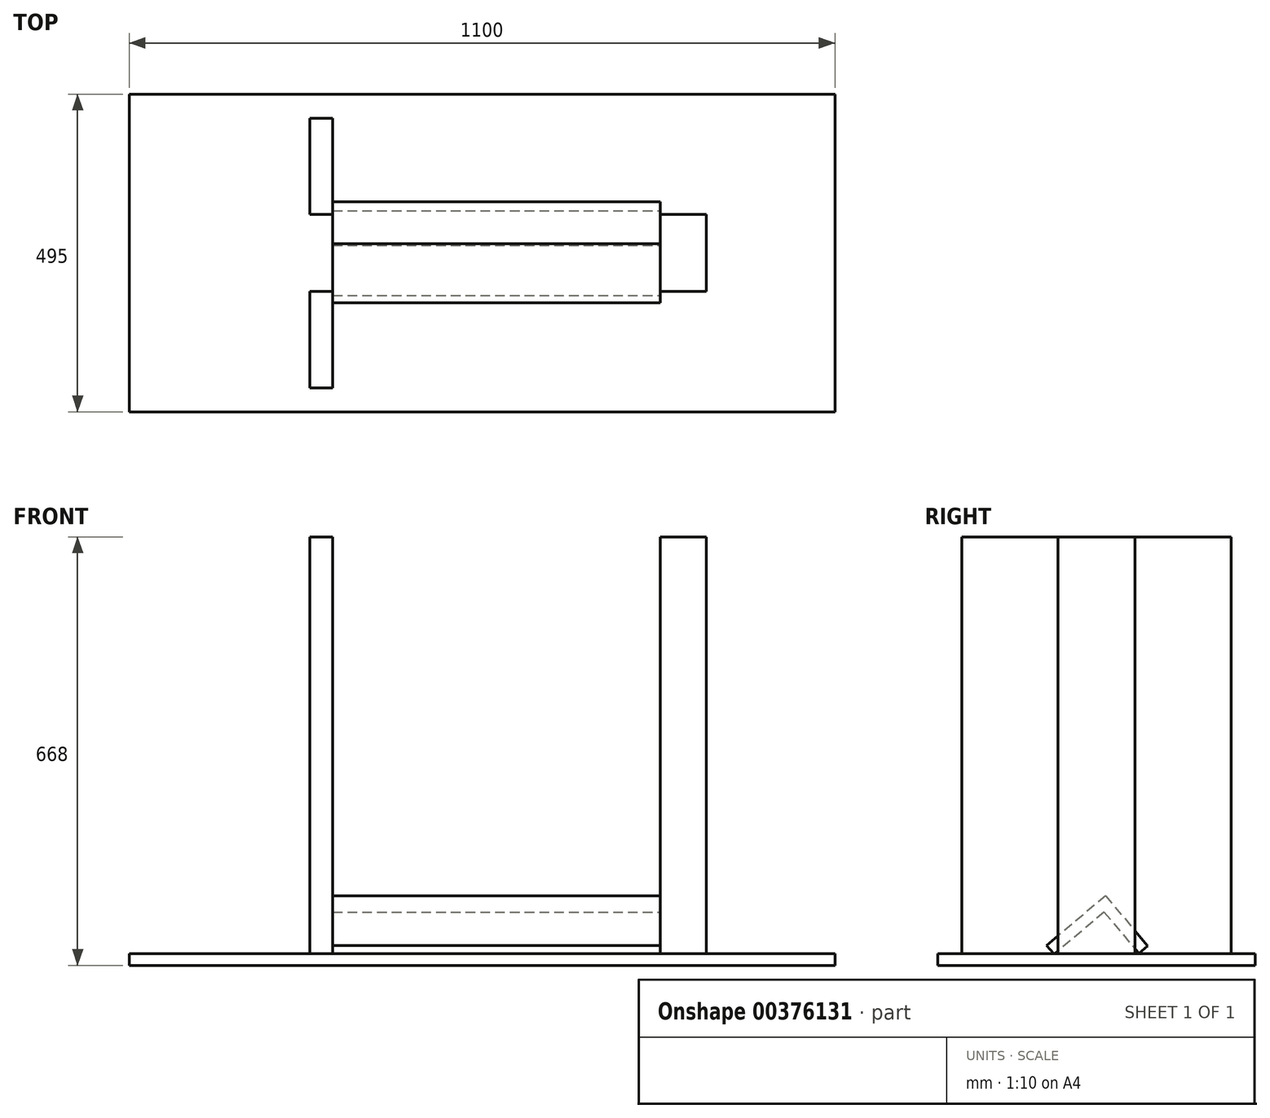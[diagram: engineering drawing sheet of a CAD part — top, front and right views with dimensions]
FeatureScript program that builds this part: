
annotation { "Feature Type Name" : "Feature", "Feature Type Description" : "" }
export const myFeature = defineFeature(function(context is Context, id is Id, definition is map)
    precondition{}
    {
        {
            var Q0;
            Q0=qCreatedBy(makeId("Top.planeOp"),FACE);
            var sketch = newSketch(context, id + "F0", { "sketchPlane" : qUnion([Q0])});
            skLineSegment(sketch, "E0.bottom", {"start": v(-550, 247.5) * mm, "end": v(550, 247.5) * mm});
            skLineSegment(sketch, "E0.top", {"start": v(-550, -247.5) * mm, "end": v(550, -247.5) * mm});
            skLineSegment(sketch, "E0.left", {"start": v(-550, 247.5) * mm, "end": v(-550, -247.5) * mm});
            skLineSegment(sketch, "E0.right", {"start": v(550, 247.5) * mm, "end": v(550, -247.5) * mm});
            skPoint(sketch, "E1", {"position": v(0, 247.5) * mm});
            skPoint(sketch, "E2", {"position": v(-550, 0) * mm});
            skSolve(sketch);
        }
        {
            var Q0;
            Q0=qSketchRegion(id+"F0",true);
            extrude(context, id + "F1", {"entities" : qUnion([Q0]), "depth" : 18 * mm, "offsetDistance" : 25 * mm});
        }
        {
            var Q0;
            Q0=makeQuery(id+"F1.opExtrude","CAP_FACE",FACE,{"disambiguationData":[OSD([sQuery(id+"F0.wireOp",EDGE,"E0.bottom"),sQuery(id+"F0.wireOp",EDGE,"E0.top"),sQuery(id+"F0.wireOp",EDGE,"E0.left"),sQuery(id+"F0.wireOp",EDGE,"E0.right")])],"isStart":false});
            var sketch = newSketch(context, id + "F2", { "sketchPlane" : qUnion([Q0])});
            skPoint(sketch, "E3", {"position": v(-550, 0) * mm});
            skLineSegment(sketch, "E4.bottom", {"start": v(-268.57, 210) * mm, "end": v(-232.57, 210) * mm});
            skLineSegment(sketch, "E4.top", {"start": v(-268.57, -210) * mm, "end": v(-232.57, -210) * mm});
            skLineSegment(sketch, "E4.left", {"start": v(-268.57, 210) * mm, "end": v(-268.57, -210) * mm});
            skLineSegment(sketch, "E4.right", {"start": v(-232.57, 210) * mm, "end": v(-232.57, -210) * mm});
            skPoint(sketch, "E5", {"position": v(-268.57, 0) * mm});
            skLineSegment(sketch, "E6.bottom", {"start": v(349.43, -60) * mm, "end": v(277.43, -60) * mm});
            skLineSegment(sketch, "E6.top", {"start": v(349.43, 60) * mm, "end": v(277.43, 60) * mm});
            skLineSegment(sketch, "E6.left", {"start": v(349.43, -60) * mm, "end": v(349.43, 60) * mm});
            skLineSegment(sketch, "E6.right", {"start": v(277.43, -60) * mm, "end": v(277.43, 60) * mm});
            skPoint(sketch, "E7", {"position": v(349.43, 0) * mm});
            skPoint(sketch, "E8", {"position": v(0, -247.5) * mm});
            skSolve(sketch);
        }
        {
            var Q0;
            {var subQ1=sQuery(id+"F2.wireOp",EDGE,"E4.bottom");Q0=makeQuery(id+"F2.imprint","IMPRINT",FACE,{"disambiguationData":[TD([[makeQuery(id+"F2.imprint","IMPRINT",EDGE,{"derivedFrom":subQ1}),-1.0]])]});}
            var Q1;
            Q1=makeQuery(id+"F2.imprint","IMPRINT",FACE,{"disambiguationData":[TD([[makeQuery(id+"F2.imprint","IMPRINT",EDGE,{"derivedFrom":sQuery(id+"F2.wireOp",EDGE,"1kVaZgk3-8Nhi-dGg9-Ba8R-nr3TmBuge7lK.bottom")}),-1.0]])]});
            var Q2;
            Q2=makeQuery(id+"F2.imprint","IMPRINT",FACE,{"disambiguationData":[TD([[makeQuery(id+"F2.imprint","IMPRINT",EDGE,{"derivedFrom":sQuery(id+"F2.wireOp",EDGE,"d1aede41-c4be-4dbf-9319-fc5a6116a92b.bottom")}),-1.0]])]});
            var Q3;
            {var subQ1=sQuery(id+"F2.wireOp",EDGE,"E6.bottom");Q3=makeQuery(id+"F2.imprint","IMPRINT",FACE,{"disambiguationData":[TD([[makeQuery(id+"F2.imprint","IMPRINT",EDGE,{"derivedFrom":subQ1}),-1.0]])]});}
            extrude(context, id + "F3", {"entities" : qUnion([Q0, Q1, Q2, Q3]), "depth" : 650 * mm, "offsetDistance" : 25 * mm});
        }
        {
            var Q0;
            Q0=makeQuery(id+"F3.opExtrude","SWEPT_FACE",FACE,{"disambiguationData":[OSD([sQuery(id+"F2.wireOp",EDGE,"E6.left")])]});
            var sketch = newSketch(context, id + "F4", { "sketchPlane" : qUnion([Q0])});
            skLineSegment(sketch, "E9.bottom", {"start": v(60, 18) * mm, "end": v(-60, 18) * mm});
            skLineSegment(sketch, "E9.top", {"start": v(60, 668) * mm, "end": v(-60, 668) * mm});
            skLineSegment(sketch, "E9.left", {"start": v(60, 18) * mm, "end": v(60, 668) * mm});
            skLineSegment(sketch, "E9.right", {"start": v(-60, 18) * mm, "end": v(-60, 668) * mm});
            skPoint(sketch, "E10", {"position": v(0, 18) * mm});
            skPoint(sketch, "E11", {"position": v(140, 18) * mm});
            skPoint(sketch, "E12", {"position": v(-140, 18) * mm});
            skPoint(sketch, "E13", {"position": v(140, 668) * mm});
            skPoint(sketch, "E14", {"position": v(-140, 668) * mm});
            skLineSegment(sketch, "E15", {"start": v(60, 18) * mm, "end": v(140, 668) * mm});
            skLineSegment(sketch, "E16", {"start": v(-140, 668) * mm, "end": v(-60, 18) * mm});
            skSolve(sketch);
        }
        {
            var Q0;
            {var subQ0=sQuery(id+"F4.wireOp",EDGE,"E9.left");Q0=makeQuery(id+"F4.imprint","IMPRINT",FACE,{"disambiguationData":[TD([[makeQuery(id+"F4.imprint","IMPRINT",EDGE,{"derivedFrom":subQ0}),-1.0]])]});}
            var Q1;
            {var subQ0=sQuery(id+"F4.wireOp",EDGE,"E9.right");Q1=makeQuery(id+"F4.imprint","IMPRINT",FACE,{"disambiguationData":[TD([[makeQuery(id+"F4.imprint","IMPRINT",EDGE,{"derivedFrom":subQ0}),1.0]])]});}
            var Q2;
            {var subQ3=sQuery(id+"F4.wireOp",EDGE,"ERWEisdO-8PsZ-Fccj-wROh-Rmm69zbihmoK");Q2=makeQuery(id+"F4.imprint","IMPRINT",FACE,{"disambiguationData":[TD([[makeQuery(id+"F4.imprint","IMPRINT",EDGE,{"derivedFrom":subQ3}),-1.0]])]});}
            var Q3;
            {var subQ3=sQuery(id+"F4.wireOp",EDGE,"njEO2kw1-x9P7-cku3-6qRM-CGIWQrq0eT6F");Q3=makeQuery(id+"F4.imprint","IMPRINT",FACE,{"disambiguationData":[TD([[makeQuery(id+"F4.imprint","IMPRINT",EDGE,{"derivedFrom":subQ3}),1.0]])]});}
            var Q4;
            {var subQ0=sQuery(id+"F4.wireOp",EDGE,"ERWEisdO-8PsZ-Fccj-wROh-Rmm69zbihmoK");Q4=makeQuery(id+"F4.imprint","IMPRINT",FACE,{"disambiguationData":[TD([[makeQuery(id+"F4.imprint","IMPRINT",EDGE,{"derivedFrom":subQ0}),1.0]])]});}
            var Q5;
            {var subQ0=sQuery(id+"F4.wireOp",EDGE,"njEO2kw1-x9P7-cku3-6qRM-CGIWQrq0eT6F");Q5=makeQuery(id+"F4.imprint","IMPRINT",FACE,{"disambiguationData":[TD([[makeQuery(id+"F4.imprint","IMPRINT",EDGE,{"derivedFrom":subQ0}),-1.0]])]});}
            extrude(context, id + "F5", {"entities" : qUnion([Q0, Q1, Q2, Q3, Q4, Q5]), "operationType" : NewBodyOperationType.REMOVE, "endBound" : BoundingType.THROUGH_ALL, "oppositeDirection" : true, "depth" : 25 * mm, "offsetDistance" : 25 * mm});
        }
        {
            var Q0;
            Q0=makeQuery(id+"F3.opExtrude","SWEPT_FACE",FACE,{"disambiguationData":[OSD([sQuery(id+"F2.wireOp",EDGE,"E4.right"),sQuery(id+"F2.wireOp",EDGE,"1kVaZgk3-8Nhi-dGg9-Ba8R-nr3TmBuge7lK.left")])]});
            var sketch = newSketch(context, id + "F6", { "sketchPlane" : qUnion([Q0])});
            skLineSegment(sketch, "E17.bottom", {"start": v(118, 18) * mm, "end": v(100, 18) * mm});
            skLineSegment(sketch, "E17.top", {"start": v(118, 120) * mm, "end": v(100, 120) * mm});
            skLineSegment(sketch, "E17.left", {"start": v(118, 18) * mm, "end": v(118, 120) * mm});
            skLineSegment(sketch, "E17.right", {"start": v(100, 18) * mm, "end": v(100, 120) * mm});
            skSolve(sketch);
        }
        {
            var Q0;
            {var subQ1=sQuery(id+"F2.wireOp",EDGE,"E6.bottom");Q0=makeQuery(id+"F2.imprint","IMPRINT",FACE,{"disambiguationData":[TD([[makeQuery(id+"F2.imprint","IMPRINT",EDGE,{"derivedFrom":subQ1}),-1.0]])]});}
            extrude(context, id + "F7", {"entities" : qUnion([Q0]), "depth" : 650 * mm, "offsetDistance" : 25 * mm});
        }
        {
            var Q0;
            Q0=makeQuery(id+"F7.opExtrude","SWEPT_FACE",FACE,{"disambiguationData":[OSD([sQuery(id+"F2.wireOp",EDGE,"E6.right")])]});
            var sketch = newSketch(context, id + "F8", { "sketchPlane" : qUnion([Q0])});
            skLineSegment(sketch, "E18.bottom", {"start": v(-14.29, 108.32) * mm, "end": v(-0.5, 96.74) * mm});
            skLineSegment(sketch, "E18.top", {"start": v(-79.85, 30.18) * mm, "end": v(-66.07, 18.6) * mm});
            skLineSegment(sketch, "E18.left", {"start": v(-14.29, 108.32) * mm, "end": v(-79.85, 30.18) * mm});
            skLineSegment(sketch, "E18.right", {"start": v(-0.5, 96.74) * mm, "end": v(-66.07, 18.6) * mm});
            skLineSegment(sketch, "E19.bottom", {"start": v(-0.5, 96.74) * mm, "end": v(77.64, 31.18) * mm});
            skLineSegment(sketch, "E19.top", {"start": v(-12.07, 82.96) * mm, "end": v(66.07, 17.4) * mm});
            skLineSegment(sketch, "E19.left", {"start": v(-0.5, 96.74) * mm, "end": v(-12.07, 82.96) * mm});
            skLineSegment(sketch, "E19.right", {"start": v(77.64, 31.18) * mm, "end": v(66.07, 17.4) * mm});
            skPoint(sketch, "E20", {"position": v(31.67, 69.75) * mm});
            skPoint(sketch, "E21", {"position": v(0, 18) * mm});
            skSolve(sketch);
        }
        {
            var Q0;
            Q0=makeQuery(id+"F8.imprint","IMPRINT",FACE,{"disambiguationData":[TD([[makeQuery(id+"F8.imprint","IMPRINT",EDGE,{"derivedFrom":sQuery(id+"F8.wireOp",EDGE,"E18.bottom")}),-1.0]])]});
            var Q1;
            Q1=makeQuery(id+"F8.imprint","IMPRINT",FACE,{"disambiguationData":[TD([[makeQuery(id+"F8.imprint","IMPRINT",EDGE,{"derivedFrom":sQuery(id+"F8.wireOp",EDGE,"E19.bottom")}),-1.0]])]});
            var Q2;
            {var subQ0=sQuery(id+"F8.wireOp",EDGE,"E18.top");Q2=makeQuery(id+"F8.imprint","IMPRINT",FACE,{"disambiguationData":[TD([[makeQuery(id+"F8.imprint","IMPRINT",EDGE,{"derivedFrom":subQ0}),1.0]])]});}
            extrude(context, id + "F9", {"entities" : qUnion([Q0, Q1, Q2]), "depth" : 510 * mm, "offsetDistance" : 25 * mm});
        }
    });
